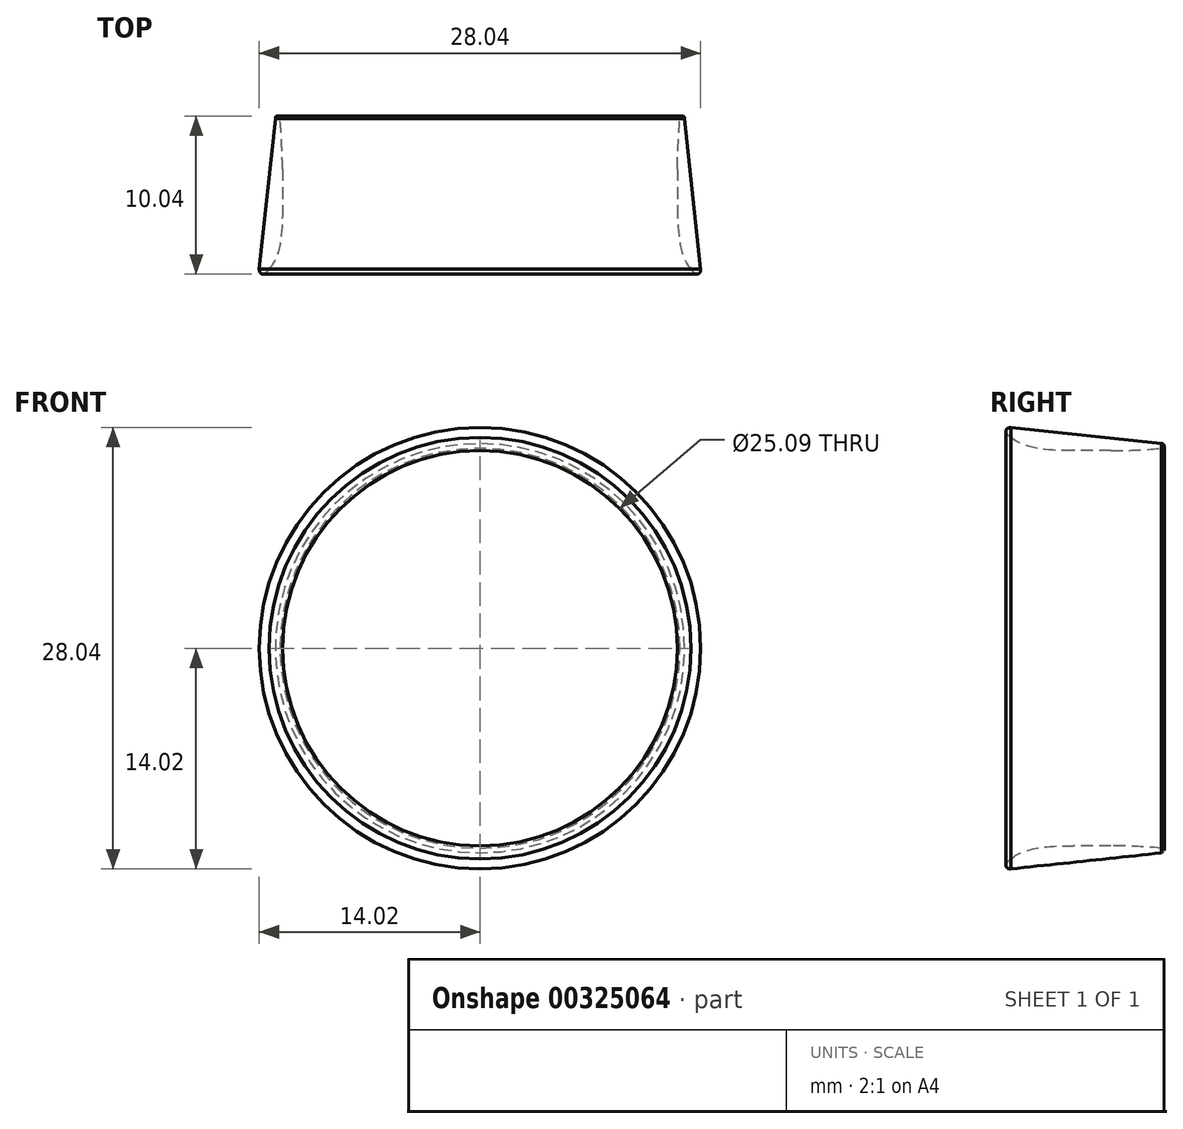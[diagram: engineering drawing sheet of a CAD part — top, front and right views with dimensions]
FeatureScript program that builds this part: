
annotation { "Feature Type Name" : "Feature", "Feature Type Description" : "" }
export const myFeature = defineFeature(function(context is Context, id is Id, definition is map)
    precondition{}
    {
        {
            var Q0;
            Q0=qCreatedBy(makeId("Right.planeOp"),FACE);
            var sketch = newSketch(context, id + "F0", { "sketchPlane" : qUnion([Q0])});
            skLineSegment(sketch, "E0", {"start": v(0, 0) * mm, "end": v(0, 12.5) * mm});
            skLineSegment(sketch, "E1", {"start": v(5.2, 14.02) * mm, "end": v(-4.38, 13) * mm});
            skLineSegment(sketch, "E2", {"start": v(-4.38, 13) * mm, "end": v(-4.38, 12.7) * mm});
            skLineSegment(sketch, "E3", {"start": v(-1.16, 12.55) * mm, "end": v(1.23, 12.55) * mm});
            skFitSpline(sketch, "E4", {"points": [v(-4.38, 12.7) * mm, v(-1.16, 12.55) * mm], "startDerivative": vector(5.58, -0.46) * mm, "endDerivative": vector(0.4, 0) * mm});
            skLineSegment(sketch, "E5", {"start": v(5.2, 14.02) * mm, "end": v(5.2, 13.4) * mm});
            skFitSpline(sketch, "E6", {"points": [v(5.2, 13.4) * mm, v(1.23, 12.55) * mm], "startDerivative": vector(-2.17, -1.85) * mm, "endDerivative": vector(-6.43, 0) * mm});
            skFitSpline(sketch, "E7", {"points": [v(-4.38, 13) * mm, v(-4.38, 12.7) * mm], "startDerivative": vector(-0.65, 0) * mm, "endDerivative": vector(0.65, 0) * mm});
            skFitSpline(sketch, "E8", {"points": [v(5.2, 14.02) * mm, v(5.2, 13.4) * mm], "startDerivative": vector(1.1, 0) * mm, "endDerivative": vector(-1.36, -0.92) * mm});
            skLineSegment(sketch, "E9", {"start": v(0, 0) * mm, "end": v(9.8, 0) * mm});
            skLineSegment(sketch, "E10", {"start": v(7.66, 10.89) * mm, "end": v(7.66, 3.33) * mm});
            skLineSegment(sketch, "E11.MirrorCS", {"start": v(10.12, 14.02) * mm, "end": v(19.69, 13) * mm});
            skFitSpline(sketch, "E12.MirrorCS", {"points": [v(10.12, 13.4) * mm, v(14.08, 12.55) * mm], "startDerivative": vector(2.17, -1.85) * mm, "endDerivative": vector(6.43, 0) * mm});
            skLineSegment(sketch, "E13.MirrorCS", {"start": v(16.48, 12.55) * mm, "end": v(14.08, 12.55) * mm});
            skFitSpline(sketch, "E14.MirrorCS", {"points": [v(19.69, 12.7) * mm, v(16.48, 12.55) * mm], "startDerivative": vector(-5.58, -0.46) * mm, "endDerivative": vector(-0.4, 0) * mm});
            skFitSpline(sketch, "E15.MirrorCS", {"points": [v(19.69, 13) * mm, v(19.69, 12.7) * mm], "startDerivative": vector(0.65, 0) * mm, "endDerivative": vector(-0.65, 0) * mm});
            skFitSpline(sketch, "E16.MirrorCS", {"points": [v(10.12, 14.02) * mm, v(10.12, 13.4) * mm], "startDerivative": vector(-1.1, 0) * mm, "endDerivative": vector(1.36, -0.92) * mm});
            skSolve(sketch);
        }
        {
            var Q0;
            Q0=makeQuery(id+"F0.imprint","IMPRINT",FACE,{"disambiguationData":[TD([[makeQuery(id+"F0.imprint","IMPRINT",EDGE,{"derivedFrom":sQuery(id+"F0.wireOp",EDGE,"E11.MirrorCS")}),-1.0]])]});
            var Q1;
            Q1=sQuery(id+"F0.wireOp",EDGE,"E9");
            revolve(context, id + "F1", {"surfaceOperationType" : NewSurfaceOperationType.NEW, "entities" : qUnion([Q0]), "axis" : qUnion([Q1]), "revolveType" : RevolveType.FULL});
        }
    });
